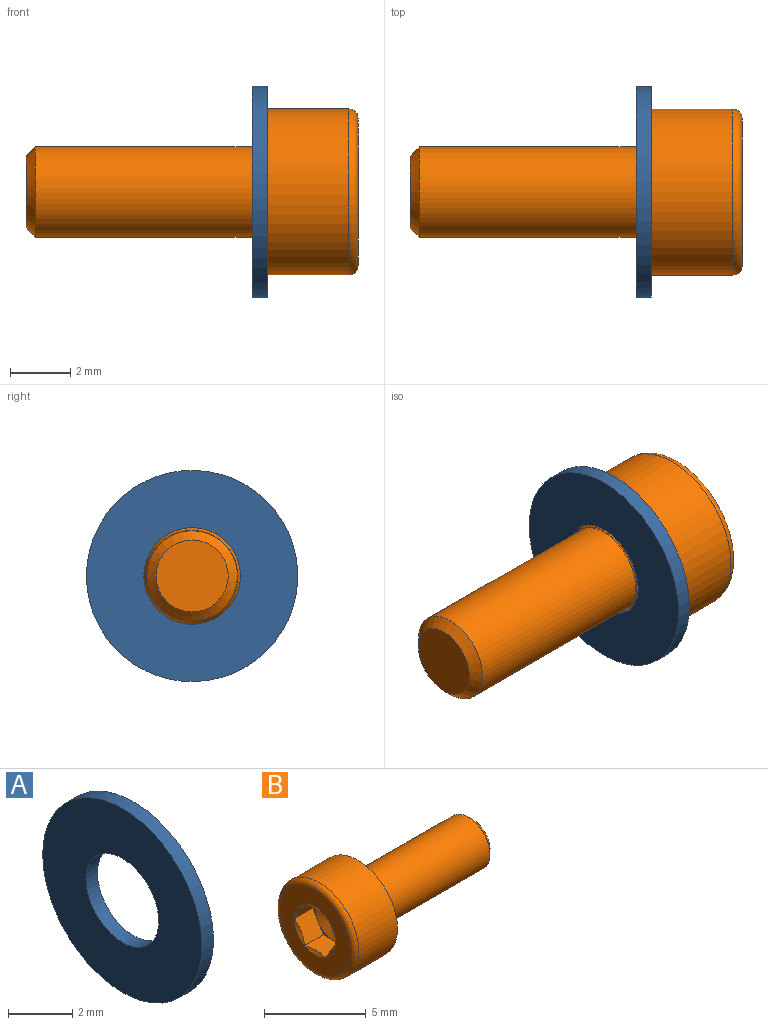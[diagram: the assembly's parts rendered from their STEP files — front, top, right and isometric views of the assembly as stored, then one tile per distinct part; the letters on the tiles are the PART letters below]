
ASSEMBLY  parts=2 mates=1
PART A: 4 faces, bbox 0.5x7x7 mm
  f0: plane 7x7mm, normal (-1,0,0), area 30.4mm2, adj f1,f3
  f1: cylinder r=1.6mm len=3.2mm, axis (1,0,0), area 5mm2, adj f0,f2
  f2: plane 7x7mm, normal (1,0,0), area 30.4mm2, adj f1,f3
  f3: cylinder r=3.5mm len=7mm, axis (1,0,0), area 11mm2, adj f0,f2
PART B: 24 faces, bbox 11x6x6 mm
  f0: plane 1.08x0.63mm, normal (-1,0,0), area 0.1mm2, adj f16,f17,f23
  f1: plane 1.25x0.36mm, normal (-1,0,0), area 0.1mm2, adj f17,f18,f23
  f2: plane 1.08x0.63mm, normal (-1,0,0), area 0.1mm2, adj f18,f19,f23
  f3: plane 1.08x0.63mm, normal (-1,0,0), area 0.1mm2, adj f19,f20,f23
  f4: plane 1.25x0.36mm, normal (-1,0,0), area 0.1mm2, adj f20,f21,f23
  f5: cone r=1.45mm half-angle=60deg, axis (-1,0,0), area 1.4mm2, adj f15,f16,f17,f18,f19,f20,f21
  f6: cone r=1.51mm half-angle=26deg, axis (-1,0,0), area 4.6mm2, adj f7,f11
  f7: torus R=1.6mm, axis (1,0,0), area 0.4mm2, adj f6,f10
  f8: plane 2.39x2.39mm, normal (1,0,0), area 4.5mm2, adj f9
  f9: cone r=1.5mm half-angle=45deg, axis (-1,0,0), area 3.7mm2, adj f8,f10
  f10: cylinder r=1.5mm len=7.18mm, axis (1,0,0), area 67.7mm2, adj f7,f9
  f11: torus R=1.8mm, axis (1,0,0), area 1.2mm2, adj f6,f13
  f12: cylinder r=2.75mm len=5.5mm, axis (1,0,0), area 46.7mm2, adj f13,f14
  f13: plane 5.5x5.5mm, normal (1,0,0), area 13.6mm2, adj f11,f12
  f14: torus R=2.45mm, axis (1,0,0), area 7.8mm2, adj f12,f15
  f15: plane 4.9x4.9mm, normal (-1,0,0), area 12.2mm2, adj f5,f14
  f16: plane 1.45x1.3mm, normal (0,0,-1), area 1.8mm2, adj f0,f5,f17,f21,f22
  f17: plane 1.29x1.25mm, normal (0,0.87,-0.5), area 1.8mm2, adj f0,f1,f5,f16,f18
  f18: plane 1.29x1.25mm, normal (0,0.87,0.5), area 1.8mm2, adj f1,f2,f5,f17,f19
  f19: plane 1.45x1.3mm, normal (0,0,1), area 1.8mm2, adj f2,f3,f5,f18,f20
  f20: plane 1.29x1.25mm, normal (0,-0.87,0.5), area 1.8mm2, adj f3,f4,f5,f19,f21
  f21: plane 1.29x1.25mm, normal (0,-0.87,-0.5), area 1.8mm2, adj f4,f5,f16,f20,f22
  f22: plane 1.08x0.63mm, normal (-1,0,0), area 0.1mm2, adj f16,f21,f23
  f23: cone r=1.25mm half-angle=60deg, axis (-1,0,0), area 5.7mm2, adj f0,f1,f2,f3,f4,f22
PLACE A at identity fixed
PLACE B rot(axis=(0,1,0),180deg) t=(0.5,0,0)mm
MATE fastened B.f5 <-> A.f1  axis (-1,0,0) through (0.5,0,0)mm
